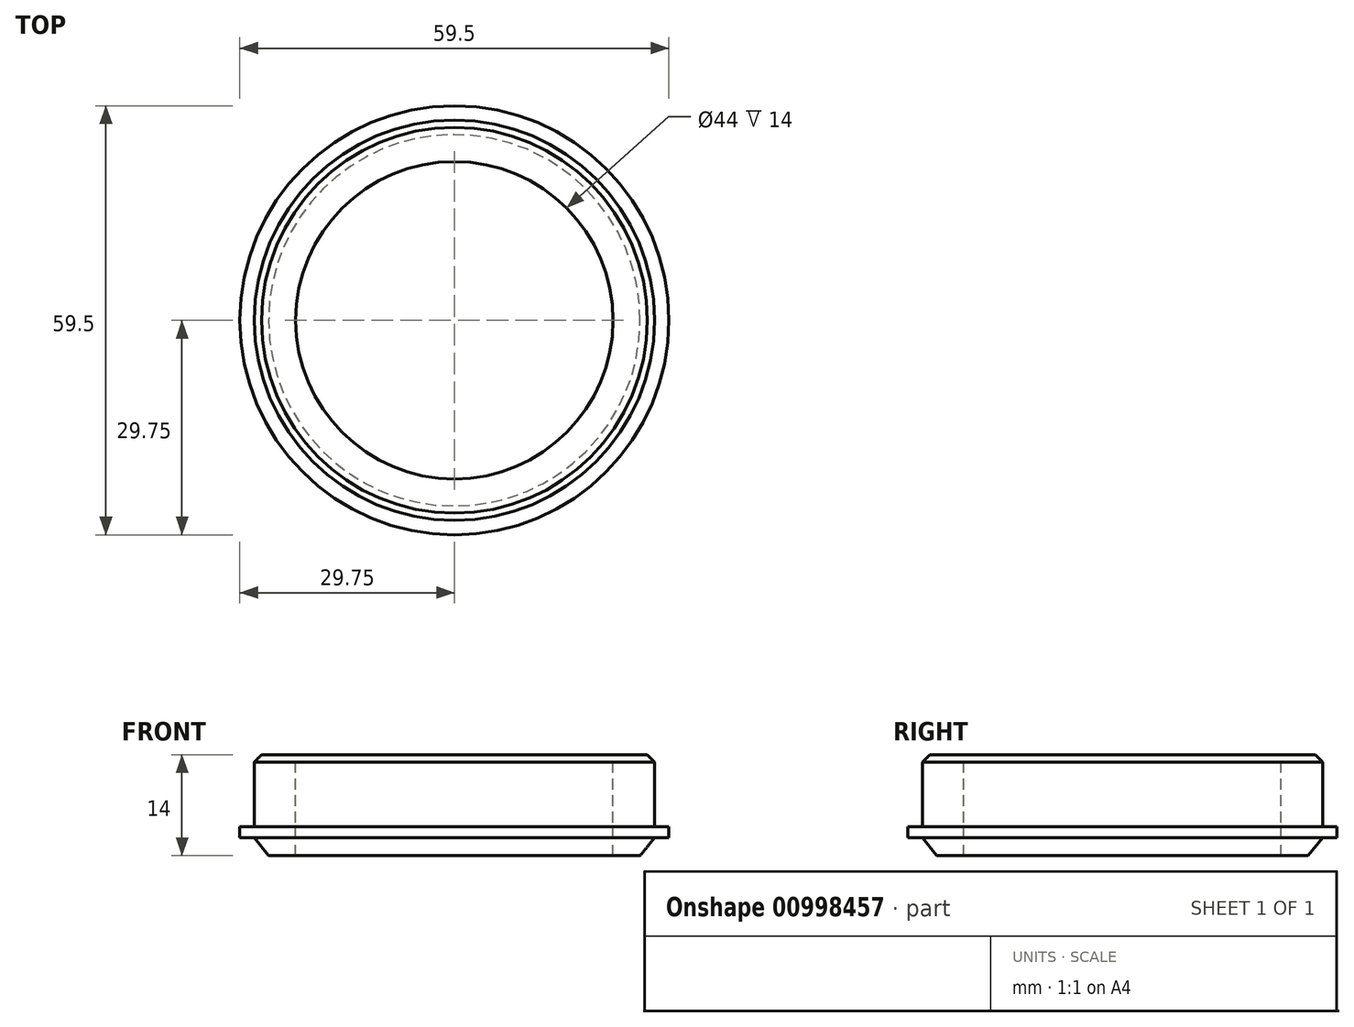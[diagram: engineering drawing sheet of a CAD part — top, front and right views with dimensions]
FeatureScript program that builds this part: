
annotation { "Feature Type Name" : "Feature", "Feature Type Description" : "" }
export const myFeature = defineFeature(function(context is Context, id is Id, definition is map)
    precondition{}
    {
        {
            var Q0;
            Q0=qCreatedBy(makeId("Front.planeOp"),FACE);
            var sketch = newSketch(context, id + "F0", { "sketchPlane" : qUnion([Q0])});
            skLineSegment(sketch, "E0", {"start": v(0, 0) * mm, "end": v(25.75, 0) * mm});
            skLineSegment(sketch, "E1", {"start": v(25.75, 0) * mm, "end": v(27.75, 2.5) * mm});
            skLineSegment(sketch, "E2", {"start": v(27.75, 2.5) * mm, "end": v(29.75, 2.5) * mm});
            skLineSegment(sketch, "E3", {"start": v(29.75, 2.5) * mm, "end": v(29.75, 4) * mm});
            skLineSegment(sketch, "E4", {"start": v(29.75, 4) * mm, "end": v(27.75, 4) * mm});
            skLineSegment(sketch, "E5", {"start": v(27.75, 4) * mm, "end": v(27.75, 14) * mm});
            skLineSegment(sketch, "E6", {"start": v(27.75, 14) * mm, "end": v(0, 14) * mm});
            skLineSegment(sketch, "E7", {"start": v(0, 14) * mm, "end": v(0, 0) * mm});
            skSolve(sketch);
        }
        {
            var Q0;
            Q0 = qSketchRegion(id + "F0", true);
            var Q1;
            Q1=sQuery(id+"F0.wireOp",EDGE,"E7");
            revolve(context, id + "F1", {"surfaceOperationType" : NewSurfaceOperationType.NEW, "entities" : qUnion([Q0]), "axis" : qUnion([Q1]), "revolveType" : RevolveType.FULL});
        }
        {
            var Q0;
            Q0=makeQuery(id+"F1.opRevolve","SWEPT_FACE",FACE,{"disambiguationData":[OSD([sQuery(id+"F0.wireOp",EDGE,"E6")])]});
            var sketch = newSketch(context, id + "F2", { "sketchPlane" : qUnion([Q0])});
            skCircle(sketch, "E8", {"center": v(0, 0) * mm, "radius": 22 * mm});
            skSolve(sketch);
        }
        {
            var Q0;
            Q0 = qSketchRegion(id + "F2", true);
            extrude(context, id + "F3", {"entities" : qUnion([Q0]), "operationType" : NewBodyOperationType.REMOVE, "oppositeDirection" : true, "depth" : 25 * mm, "offsetDistance" : 25 * mm});
        }
        {
            var Q0;
            Q0=makeQuery(id+"F1.opRevolve","SWEPT_EDGE",EDGE,{"disambiguationData":[OSD([sQuery(id+"F0.wireOp",EDGE,"E5"),sQuery(id+"F0.wireOp",EDGE,"E6")])]});
            chamfer(context, id + "F4", {"entities" : qUnion([Q0]), "width" : 1 * mm, "tangentPropagation" : true});
        }
    });
